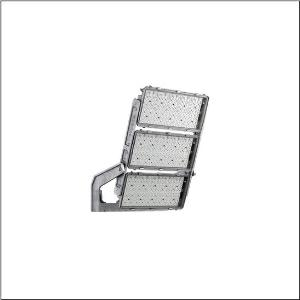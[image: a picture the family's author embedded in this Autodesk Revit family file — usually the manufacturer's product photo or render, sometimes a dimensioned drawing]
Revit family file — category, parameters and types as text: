
# Revit family: floodlight_fl_11_maxi_pro_remote___pl33t_5xa779427t01aa_b0c2
name_source: partatom
category: Lighting Fixtures
units: mm (PartAtom-declared; Revit-internal decimal feet)

## family parameters
Cut with Voids When Loaded = No
Host = Face
Light Source = No
Part Type = Normal
Room Calculation Point = No
Round Connector Dimension = Use Diameter
Shared = No

## types (1)
- --- (1 x LED, 215350 lm, 1540.1 W, 5000K)
    Apparent Load = 1540 VA
    CIE Flux Codes = 27 70 98 100 100
    Color Rendering = 70
    Color Temperature = 5000K
    Default Elevation = 1800 mm
    Description = Floodlight FL 11  maxi  pro Remote floodlight; light control with lens of PMMA; cover panel of toughened safety glass, transparent; light distribution: PL33T, asymmetric direct distribution, LEDcolour temperature: 5000K, rated luminous flux: 215.350lm, colour rendering: CRI > 70, light colour: 750; luminous efficacy: 140lm/W; brightness control: DALI 2 (1 DALI address); with terminal, 8-pole, max. 2.5mm², mains connection: 220..240V/380..400V AC, 50/60Hz, surge voltage resistance: line to ground: 10kV, ECG replaceable separately, no afterglow with DALI off / DMX off command, LED unit replaceable without ESD environment, dustproof LED module, dimming range 10..100%; 1540W floodlight with 2x LED unit of diecast aluminium, coated grey; length: 713mm / width: 651mm / height: 338mm; mounting bracket, of diecast aluminium, uncoated, natural, equipment: Power, protection rating (complete): IP66; insulation class (complete): insulation class I (protective earthing); certification: CE, ENEC, VDE; ball protection: ball impact resistance with accessories, impact resistance: IK07; only for outdoor installations, rated ambient temperature 10°C, permissible operating ambient temperature: -40..+30°C, permissible storage temperature: -40..+85°C; packaging unit: 1 piece

Light Distribution: PL33T
    Height = 320 mm
    Lamp = 1 x LED
    Lamp Light Flux = 215350 lm
    Lamp Power = 1540.1 W
    Lamp count = 1
    Length = 1002 mm
    Luminous efficacy = 140 lm/W
    Manufacturer = Siteco
    ModVariant = No
    Model = 5XA779427T01AA
    Mounting Place = Ceiling
    Mounting Type = Surface mounted
    Number of Poles = 1
    OnlyDefault = Yes
    Power Factor = 1
    Product Name = Floodlight FL 11 maxi pro Remote | PL33T
    Product group = floodlight | ceiling mounted
    ProductGroupID = 303
    Protection Class = Protection class I
    Protection Degree = IP 66
    RLX_Detail_Level = 1
    RLX_Emergency_Light_Flux = 0 lm
    RLX_Emergency_Type = 0
    RLX_Emergency_Type_DB = No
    RlxData = <blob elided: 52277 chars, md5=9257872a>
    Socket = socket
    Standby Power = 0 W
    System Light Flux = 215350 lm
    System Power = 1540 W
    Type Comments = factory setting: luminous flux: 100 % | dim-lin: 254 | 1080 mA
    Type Image = l_1006784.jpg
    URL = http://relux.com
    VarID = @adj_030791
    Voltage = 0 V
    Weight = 0.00 kg
    Width = 655 mm

## geometry (parser evidence)
native form markers: Blend x4, Sweep x16
no freeform markers — native parametric forms only
